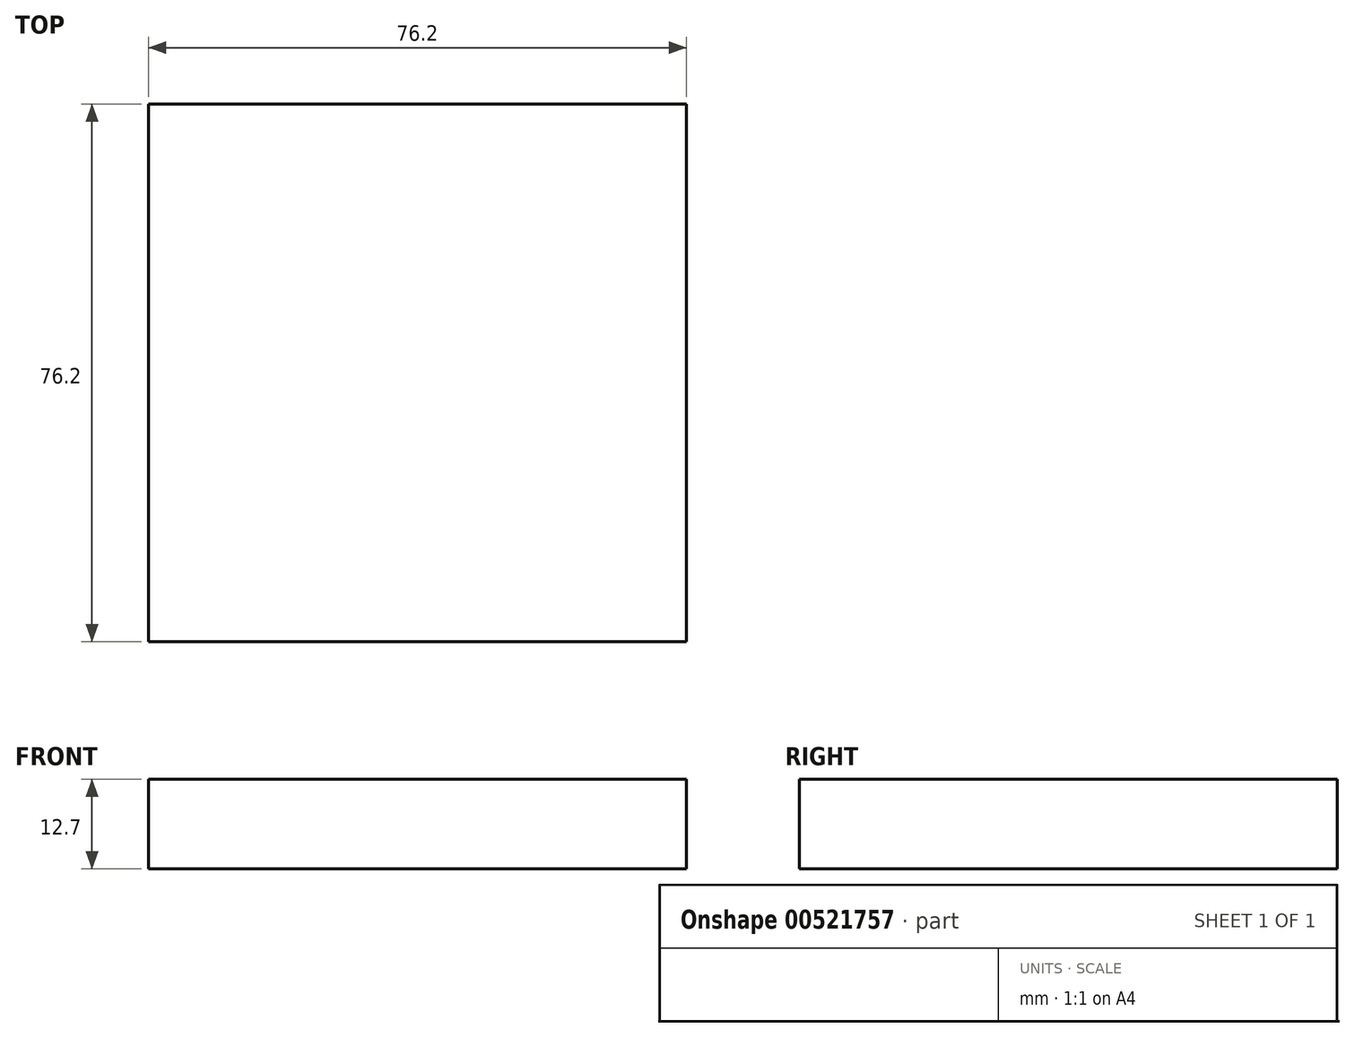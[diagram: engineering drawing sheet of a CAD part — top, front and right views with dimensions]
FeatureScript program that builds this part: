
annotation { "Feature Type Name" : "Feature", "Feature Type Description" : "" }
export const myFeature = defineFeature(function(context is Context, id is Id, definition is map)
    precondition{}
    {
        {
            var Q0;
            Q0=qCreatedBy(makeId("Top.planeOp"),FACE);
            var sketch = newSketch(context, id + "F0", { "sketchPlane" : qUnion([Q0])});
            skLineSegment(sketch, "E0.bottom", {"start": v(0, 0) * mm, "end": v(76.2, 0) * mm});
            skLineSegment(sketch, "E0.top", {"start": v(0, 76.2) * mm, "end": v(76.2, 76.2) * mm});
            skLineSegment(sketch, "E0.left", {"start": v(0, 0) * mm, "end": v(0, 76.2) * mm});
            skLineSegment(sketch, "E0.right", {"start": v(76.2, 0) * mm, "end": v(76.2, 76.2) * mm});
            skSolve(sketch);
        }
        {
            var Q0;
            Q0 = qSketchRegion(id + "F0", true);
            extrude(context, id + "F1", {"entities" : qUnion([Q0]), "depth" : 12.7 * mm, "offsetDistance" : 25.4 * mm});
        }
    });
